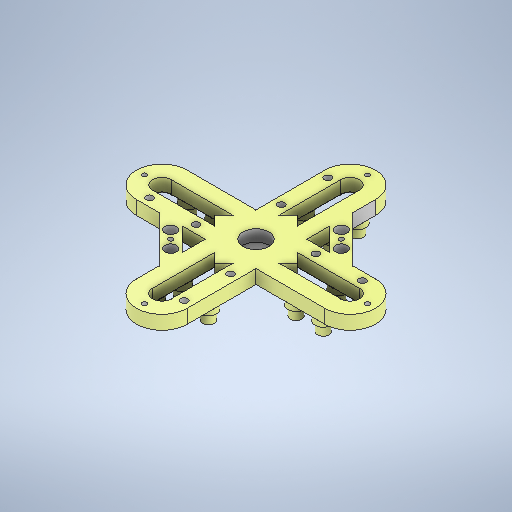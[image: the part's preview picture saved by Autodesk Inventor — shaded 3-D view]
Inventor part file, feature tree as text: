
AUTODESK INVENTOR PART (.ipt)
format: ipt  version: 2025.1 (Build 291241000, 241)  size: 1,436,160 bytes
history: native  units: in
note: dims shown in document units (in); Inventor stores cm internally (conversion verified against a paired STEP export)
features: sketch x17, extrude x12, plane x1, fillet x1, other x1
ambient origin geometry x8: Origin, YZ Plane, XZ Plane, XY Plane, X Axis, Y Axis, Z Axis, Center Point
bodies: Solid1 (feature_tree)
feature tree (32):
  sketch  "Sketch1"  dims[d12=1.0in d15=1.0in]
  extrude  "Extrusion1"  Depth=1.0in
  extrude  "Extrusion2"  TaperAngle=135.0deg  [1 undecoded]
  extrude  "Extrusion3"  Depth=1.5748in TaperAngle=360.0deg
  extrude  "Extrusion4"  Depth=0.2362in TaperAngle=0.0deg
  extrude  "Extrusion5"  Depth=0.2756in
  plane  "Work Plane1"
  sketch  "Sketch9"  dims[d84=0.4134in d87=45.0deg]
  extrude  "Extrusion12"  Depth=1.5748in TaperAngle=360.0deg
  extrude  "Extrusion13"  Depth=0.0787in
  extrude  "Extrusion14"  Depth=0.0787in
  extrude  "Extrusion15"  Depth=0.2362in TaperAngle=0.0deg
  extrude  "Extrusion16"  Depth=0.1969in TaperAngle=0.0deg
  fillet  "Fillet1"  Radius=0.1181in
  extrude  "Extrusion17"  TaperAngle=45.0deg  [1 undecoded]
  extrude  "Extrusion18"  Depth=0.4134in
  sketch  "Sketch Circular Pattern1"  dims[d18=0.1in d19=135.0deg]
  sketch  "Sketch2"  dims[d25=0.1969in d39=1.5748in d41=360.0deg]
  sketch  "Sketch Circular Pattern2"  dims[d43=0.2362in d44=0.0in d45=0.2598in d46=0.0in]
  sketch  "Sketch3"  dims[d47=0.2756in d48=0.2756in]
  sketch  "Sketch Circular Pattern3"  dims[d49=0.2756in d50=1.5748in d52=360.0deg]
  sketch  "Sketch4"  dims[d54=0.0984in d55=0.0in d56=0.0787in]
  sketch  "Sketch Circular Pattern4"  dims[d57=0.0787in d58=0.0787in]
  sketch  "Sketch11"  dims[d88=0.1181in d89=0.4134in]
  sketch  "Sketch12"  dims[d94=1.5748in d96=360.0deg]
  sketch  "Sketch13"  dims[d98=0.3937in d99=0.0in]
  sketch  "Sketch14"  dims[d100=0.3937in]
  sketch  "Sketch Circular Pattern5"  dims[d59=1.5748in d61=360.0deg d63=0.2362in d64=0.0in]
  sketch  "Sketch15"  dims[d101=0.3937in]
  sketch  "Sketch Circular Pattern6"  dims[d65=0.437in d66=0.1969in d67=0.0in d83=0.1181in]
  sketch  "Sketch16"  dims[d102=0.3937in d103=0.3937in d108=0.3937in d109=0.0in d110=0.1969in d111=0.1969in d112=0.1969in d113=0.1969in d114=0.1969in d115=0.1969in d116=0.1969in d117=0.1969in d118=0.0in d119=0.0in d120=0.1181in d121=0.0in d122=0.0787in d123=1.5748in d125=360.0deg d127=0.3937in d128=0.0in d129=0.0197in d130=0.1181in d131=1.5748in d133=360.0deg d135=0.3937in d136=0.0in d137=0.0787in d138=0.0787in d139=0.3937in d140=0.0in d92=0.0197in d93=0.0344in d95=0.0344in]
  other  "Finish1"
note: 2 required parameter values undecoded (feature->parameter linkage not recoverable at this tier; creation-order binding heuristic only, values carry confidence <= 0.55)
